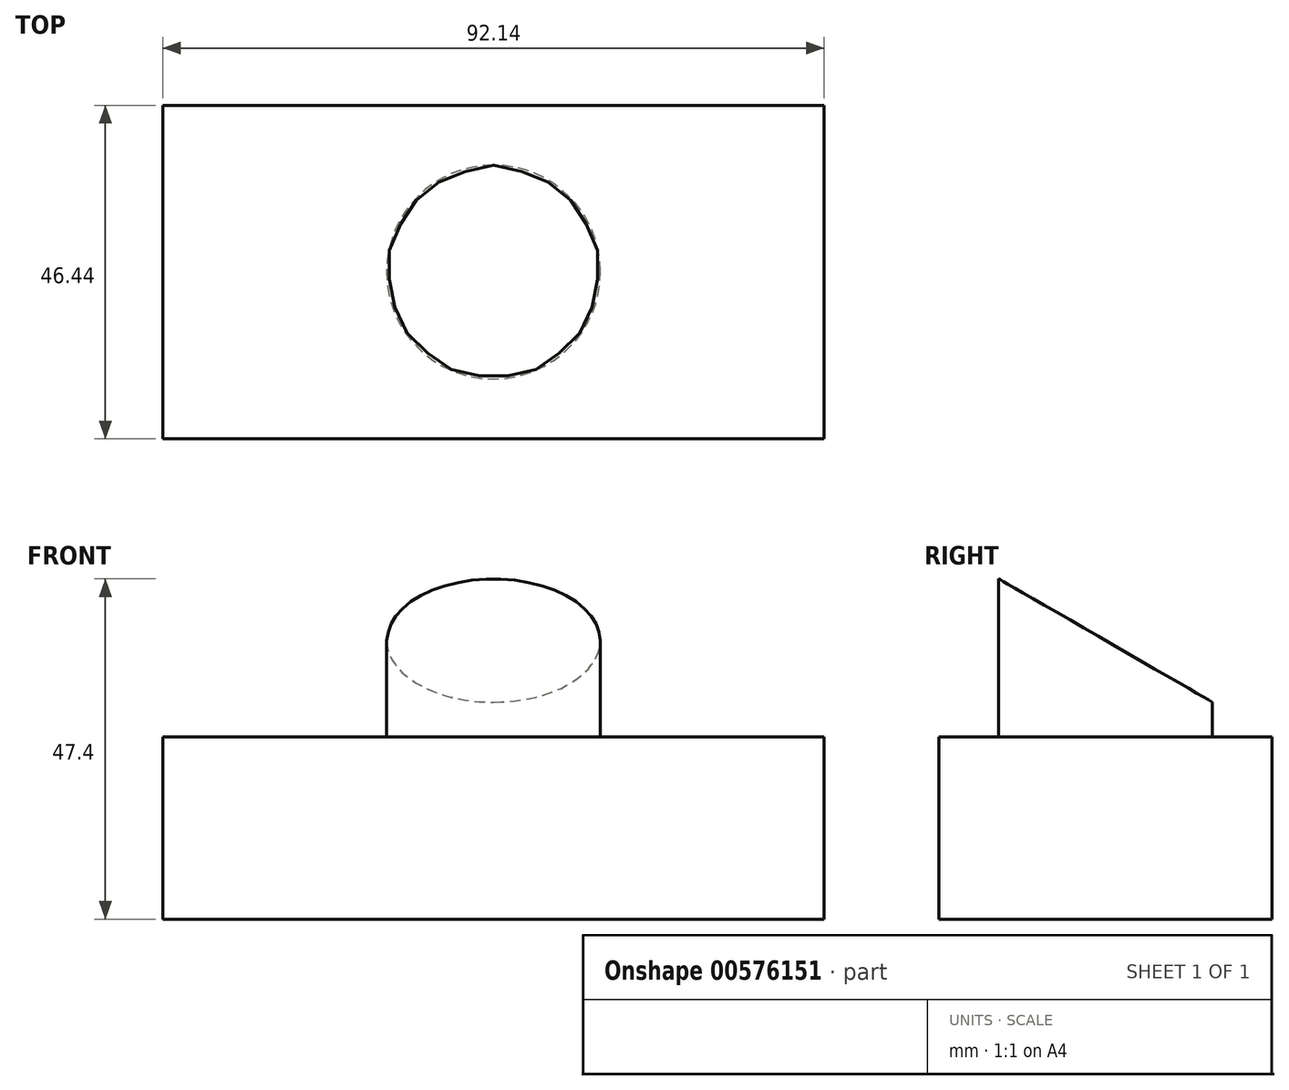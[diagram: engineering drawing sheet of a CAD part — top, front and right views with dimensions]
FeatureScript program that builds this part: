
annotation { "Feature Type Name" : "Feature", "Feature Type Description" : "" }
export const myFeature = defineFeature(function(context is Context, id is Id, definition is map)
    precondition{}
    {
        {
            var Q0;
            Q0=qCreatedBy(makeId("Top.planeOp"),FACE);
            var sketch = newSketch(context, id + "F0", { "sketchPlane" : qUnion([Q0])});
            skLineSegment(sketch, "E0.bottom", {"start": v(46.07, 23.22) * mm, "end": v(-46.07, 23.22) * mm});
            skLineSegment(sketch, "E0.top", {"start": v(46.07, -23.22) * mm, "end": v(-46.07, -23.22) * mm});
            skLineSegment(sketch, "E0.left", {"start": v(46.07, 23.22) * mm, "end": v(46.07, -23.22) * mm});
            skLineSegment(sketch, "E0.right", {"start": v(-46.07, 23.22) * mm, "end": v(-46.07, -23.22) * mm});
            skPoint(sketch, "E0.middle", {"position": v(0, 0) * mm});
            skSolve(sketch);
        }
        {
            var Q0;
            Q0 = qSketchRegion(id + "F0", true);
            extrude(context, id + "F1", {"entities" : qUnion([Q0]), "depth" : 25.4 * mm, "offsetDistance" : 25.4 * mm});
        }
        {
            var Q0;
            Q0=makeQuery(id+"F1.opExtrude","CAP_FACE",FACE,{"disambiguationData":[OSD([sQuery(id+"F0.wireOp",EDGE,"E0.bottom"),sQuery(id+"F0.wireOp",EDGE,"E0.top"),sQuery(id+"F0.wireOp",EDGE,"E0.left"),sQuery(id+"F0.wireOp",EDGE,"E0.right")])],"isStart":false});
            var sketch = newSketch(context, id + "F2", { "sketchPlane" : qUnion([Q0])});
            skCircle(sketch, "E1", {"center": v(0, 0) * mm, "radius": 14.9 * mm});
            skSolve(sketch);
        }
        {
            var Q0;
            Q0=qCreatedBy(makeId("Top.planeOp"),FACE);
            var Q1;
            Q1=makeQuery(id+"F1.opExtrude","CAP_EDGE",EDGE,{"disambiguationData":[OSD([sQuery(id+"F0.wireOp",EDGE,"E0.bottom")])],"isStart":false});
            cPlane(context, id + "F3", {"entities" : qUnion([Q0, Q1]), "cplaneType" : CPlaneType.LINE_ANGLE, "offset" : 25.4 * mm, "angle" : 30 * degree, "width" : 152.4 * mm, "height" : 152.4 * mm});
        }
        {
            var Q0;
            Q0=makeQuery(id+"F2.imprint","IMPRINT",FACE,{"disambiguationData":[TD([[makeQuery(id+"F2.imprint","IMPRINT",EDGE,{"derivedFrom":sQuery(id+"F2.wireOp",EDGE,"E1")}),1.0]])]});
            var Q1;
            Q1=qCreatedBy(id+"F3.planeOp",FACE);
            extrude(context, id + "F4", {"entities" : qUnion([Q0]), "operationType" : NewBodyOperationType.ADD, "endBound" : BoundingType.UP_TO_SURFACE, "depth" : 25.4 * mm, "endBoundEntityFace" : qUnion([Q1]), "offsetDistance" : 25.4 * mm});
        }
    });
